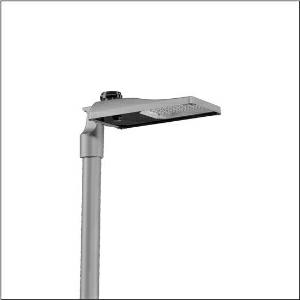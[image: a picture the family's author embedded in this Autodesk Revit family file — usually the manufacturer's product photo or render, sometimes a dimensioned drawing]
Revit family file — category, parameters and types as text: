
# Revit family: streetlight_sl_31_mini___st1_0a_5xh6d3bm08ha_d052
name_source: partatom
category: Lighting Fixtures
units: mm (PartAtom-declared; Revit-internal decimal feet)

## family parameters
Cut with Voids When Loaded = No
Host = Face
Light Source = No
Part Type = Normal
Room Calculation Point = No
Round Connector Dimension = Use Diameter
Shared = No

## types (1)
- --- (1 x LED, 9230 lm, 68.3 W, 3000K)
    Apparent Load = 68 VA
    CIE Flux Codes = 37 72 97 100 100
    Color Rendering = 70
    Color Temperature = 3000K
    Default Elevation = 1800 mm
    Description = Streetlight SL 31 mini NEMA (7pin) mast luminaire for post-top, side-entry; light control with lens of PMMA; light distribution: ST1.0a, direct asymmetric distribution, for standard-compliant lighting for roads and squares; LED: luminous flux: 9.230lm, light colour: 730, colour temperature: 3000K; luminous efficacy: 135,1lm/W; control: pre-setting: linear dimming characteristic, flexible luminous flux parameterisation, time-dependent luminous flux control, constant luminous flux control, intelligent temperature release in ECG and LED module, overheat protection; luminaire housing, of diecast aluminium, Siteco® metallic grey (DB 702S), corrosivity category C5 high according to DIN EN ISO 12944; cover of toughened safety glass, transparent, opened without tools; mast flange of diecast aluminium, Siteco® metallic grey (DB 702S), spigot size: 76/60mm, mast flange included unmounted; with cable H07RN-F 3x 1.5mm², cable length: 8,5m, connection cable pre-assembled; mains connection: 220..240V, AC, 50/60Hz; power consumption (at start of service life): 68,3W / (at end of service life): 74,5W / (with reduced operation 50%): 29,5W; protection rating (complete): IP66; insulation class (complete): insulation class I (protective earthing); impact resistance: IK09; certification: CE, ENEC, ENEC+, VDE, UKCA; permissible operating ambient temperature for outdoor applications: -40..+50°C; packaging unit: 1 piece

Light Distribution: ST1.0a
    Height = 76 mm
    Lamp = 1 x LED
    Lamp Light Flux = 9230 lm
    Lamp Power = 68.3 W
    Lamp count = 1
    Length = 547 mm
    Luminous efficacy = 135 lm/W
    Manufacturer = Siteco
    ModVariant = No
    Model = 5XH6D3BM08HA
    Number of Poles = 1
    OnlyDefault = Yes
    Power Factor = 1
    Product Name = Streetlight SL 31 mini | ST1.0a
    Product group = mast luminaire | pylon top
    ProductGroupID = 6100
    Protection Class = Protection class I
    Protection Degree = IP 66
    RLX_Detail_Level = 1
    RLX_Emergency_Light_Flux = 0 lm
    RLX_Emergency_Type = 0
    RLX_Emergency_Type_DB = No
    RlxData = <blob elided: 24801 chars, md5=4d8a7298>
    Socket = socket
    Standby Power = 0 W
    System Light Flux = 9230 lm
    System Power = 68 W
    Type Comments = factory setting: luminous flux: 100 % | dim-lin: 254 | 692 mA
    Type Image = l_1300324.jpg
    URL = http://relux.com
    VarID = @adj_001755
    Voltage = 0 V
    Weight = 0.00 kg
    Width = 265 mm

## geometry (parser evidence)
native form markers: Blend x4, Sweep x10
no freeform markers — native parametric forms only
